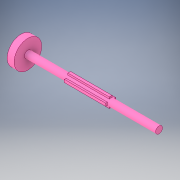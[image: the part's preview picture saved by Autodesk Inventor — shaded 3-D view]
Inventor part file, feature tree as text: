
AUTODESK INVENTOR PART (.ipt)
format: ipt  version: 2019.3 (Build 233278000, 278)  size: 142,848 bytes
history: native  units: in
note: dims shown in document units (in); Inventor stores cm internally (conversion verified against a paired STEP export)
features: extrude x4, sketch x4, plane x1
ambient origin geometry x8: Origin, YZ Plane, XZ Plane, XY Plane, X Axis, Y Axis, Z Axis, Center Point
bodies: Solid1 (feature_tree)
feature tree (9):
  extrude  "Extrusion1"  Depth=5.0in TaperAngle=0.0deg
  extrude  "Extrusion2"  Depth=0.25in TaperAngle=0.0deg
  extrude  "Extrusion3"  Depth=1.5748in TaperAngle=360.0deg
  plane  "Work Plane1"
  extrude  "Extrusion4"  Depth=1.5in
  sketch  "Sketch2"  dims[d0=0.25in d1=5.0in d2=0.0in]
  sketch  "Sketch3"  dims[d3=1.0in d4=0.25in d5=0.0in]
  sketch  "Sketch4"  dims[d7=0.05in d8=1.5748in d10=360.0deg]
  sketch  "Sketch5"  dims[d12=3.0in d13=0.0in d15=0.055in d16=1.5in d17=1.5in d18=0.0in]
